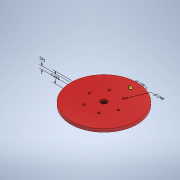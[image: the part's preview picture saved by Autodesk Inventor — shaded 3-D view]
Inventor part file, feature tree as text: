
AUTODESK INVENTOR PART (.ipt)
format: ipt  version: 2022.2 (Build 262287010, 287A)  size: 1,254,400 bytes
history: native  units: in
note: dims shown in document units (in); Inventor stores cm internally (conversion verified against a paired STEP export)
features: other x5, sketch x4, extrude x2, hole x2, revolve x1, fillet x1
ambient origin geometry x8: Origin, YZ Plane, XZ Plane, XY Plane, X Axis, Y Axis, Z Axis, Center Point
bodies: Solid1 (feature_tree)
feature tree (15):
  other  "Annotations"
  revolve  "Revolution1"  [1 undecoded]
  extrude  "ExtrusionForText"  TaperAngle=90.0deg  [1 undecoded]
  hole  "Hole6"  [1 undecoded]
  fillet  "Fillet2"  Radius=0.425in
  hole  "Hole7"  [1 undecoded]
  extrude  "Extrusion8"  Depth=0.05in
  sketch  "Sketch5"  dims[d0=4.0in d3=0.375in]
  sketch  "Sketch13"  dims[d4=1.378in d5=90.0deg]
  sketch  "Sketch16"  dims[d16=0.05in d17=0.0in d18=6.0in d64=0.425in]
  sketch  "Sketch18"  dims[d65=1.75in d66=2.3622in d68=360.0deg d70=0.249in d71=0.75in d72=0.2791in d73=0.2411in d74=0.5635in d75=1.0in d76=0.8108in d77=0.05in d94=0.472in d95=0.75in d96=0.75in d97=0.709in d98=0.5635in d99=1.0in d100=0.8108in d104=0.6793in d105=1.315in d106=0.0in d107=0.346in d108=0.1167in d109=1.315in d41=0.375in d80=1.6762in d81=0.249in d84=2.1803in d85=0.2791in d6=0.0344in]
  other  "Linear Dimension 2"
  other  "Diameter Dimension 1"
  other  "Diameter Dimension 2"
  other  "Linear Dimension 3"
note: 4 required parameter values undecoded (feature->parameter linkage not recoverable at this tier; creation-order binding heuristic only, values carry confidence <= 0.55)